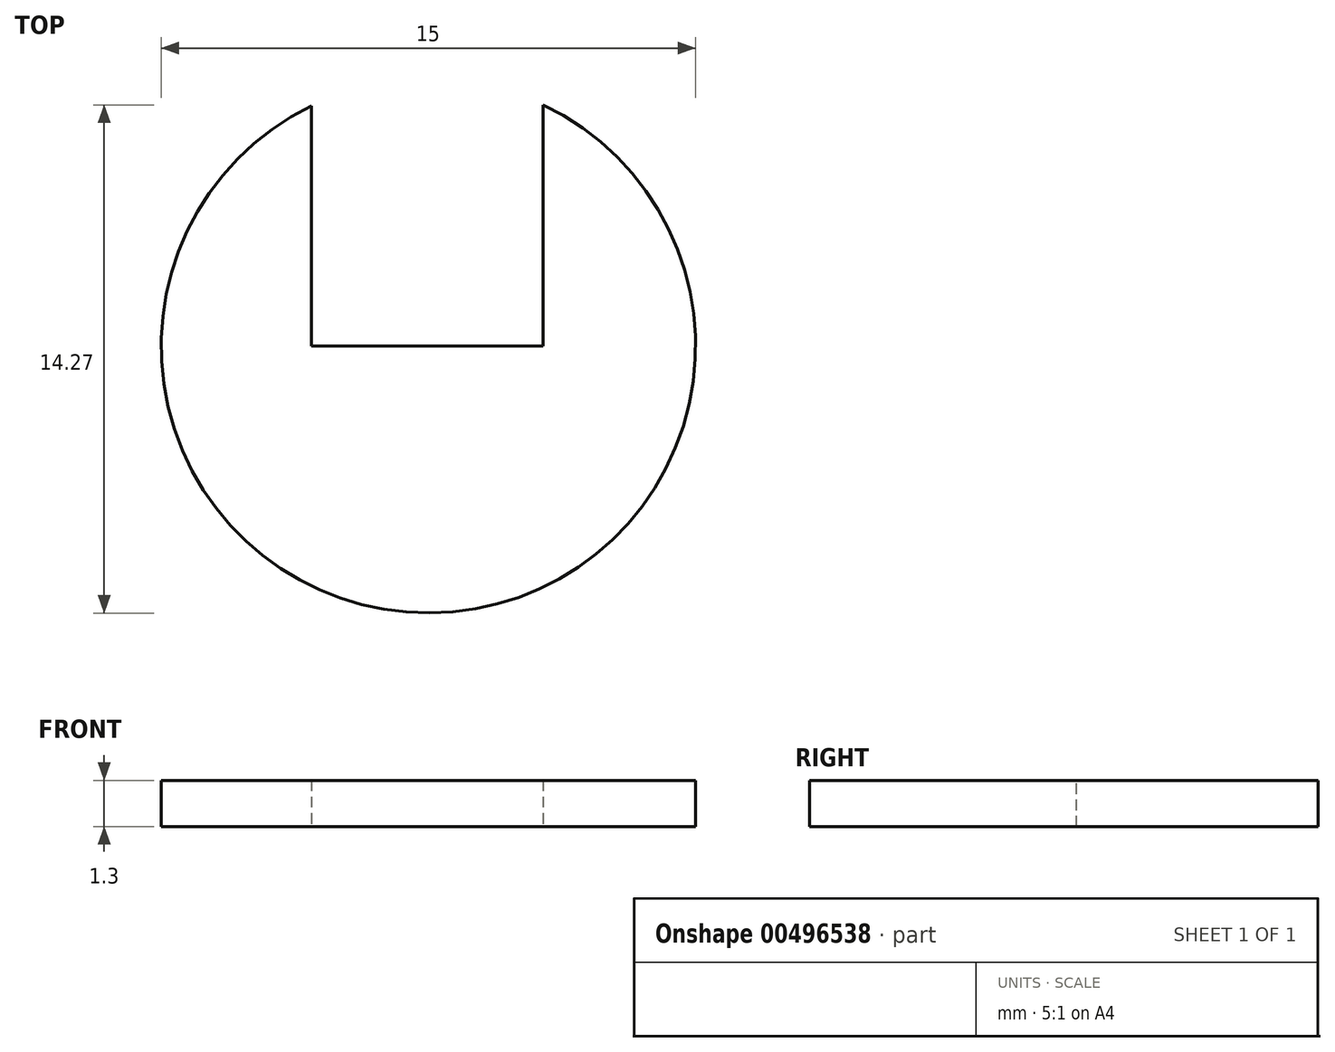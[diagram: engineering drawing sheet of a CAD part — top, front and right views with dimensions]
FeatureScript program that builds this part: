
annotation { "Feature Type Name" : "Feature", "Feature Type Description" : "" }
export const myFeature = defineFeature(function(context is Context, id is Id, definition is map)
    precondition{}
    {
        {
            var Q0;
            Q0=qCreatedBy(makeId("Top.planeOp"),FACE);
            var sketch = newSketch(context, id + "F0", { "sketchPlane" : qUnion([Q0])});
            skCircle(sketch, "E0", {"center": v(0, 0) * mm, "radius": 7.5 * mm});
            skSolve(sketch);
        }
        {
            var Q0;
            Q0=qSketchRegion(id+"F0",true);
            extrude(context, id + "F1", {"entities" : qUnion([Q0]), "depth" : 1.3 * mm, "offsetDistance" : 25 * mm});
        }
        {
            var Q0;
            Q0=makeQuery(id+"F1.opExtrude","CAP_FACE",FACE,{"disambiguationData":[OSD([sQuery(id+"F0.wireOp",EDGE,"E0")])],"isStart":false});
            var sketch = newSketch(context, id + "F2", { "sketchPlane" : qUnion([Q0])});
            skLineSegment(sketch, "E1", {"start": v(0, 0) * mm, "end": v(-0.28, 0) * mm});
            skLineSegment(sketch, "E2", {"start": v(-3.28, 0) * mm, "end": v(3.22, 0) * mm});
            skLineSegment(sketch, "E3", {"start": v(-3.28, 8.7) * mm, "end": v(2.82, 9.07) * mm});
            skLineSegment(sketch, "E4", {"start": v(-3.28, 0) * mm, "end": v(-3.28, 8.7) * mm});
            skLineSegment(sketch, "E5", {"start": v(3.22, 0) * mm, "end": v(3.22, 9.92) * mm});
            skLineSegment(sketch, "E6", {"start": v(3.22, 9.92) * mm, "end": v(2.82, 9.07) * mm});
            skSolve(sketch);
        }
        {
            var Q0;
            Q0=qSketchRegion(id+"F2",true);
            extrude(context, id + "F3", {"entities" : qUnion([Q0]), "operationType" : NewBodyOperationType.REMOVE, "oppositeDirection" : true, "depth" : 10 * mm, "offsetDistance" : 25 * mm});
        }
    });
